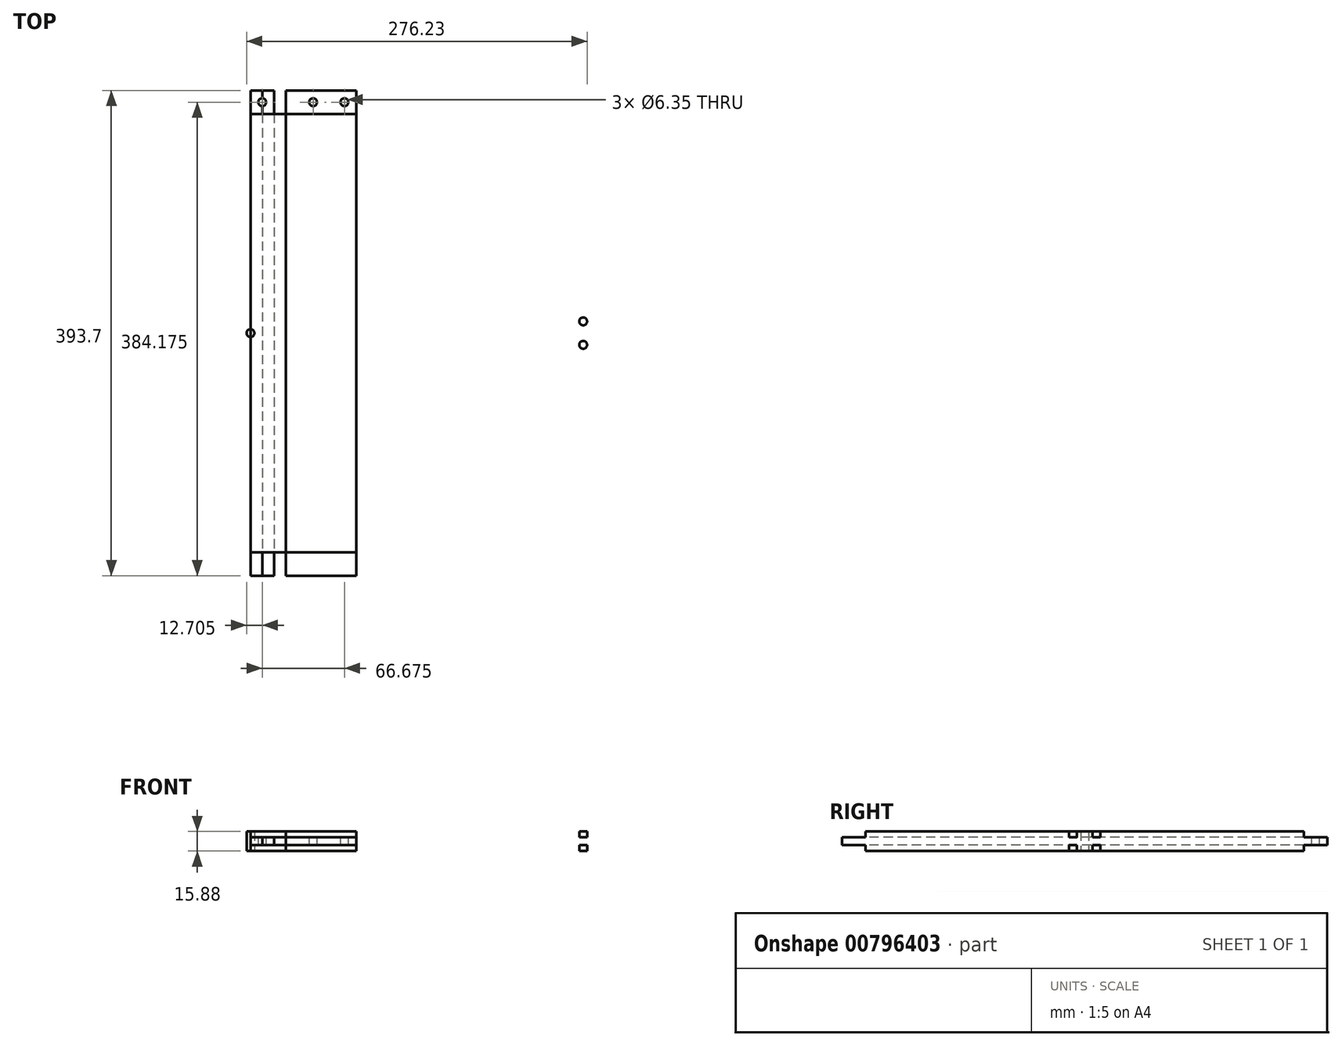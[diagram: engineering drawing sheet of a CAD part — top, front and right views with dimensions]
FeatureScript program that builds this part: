
annotation { "Feature Type Name" : "Feature", "Feature Type Description" : "" }
export const myFeature = defineFeature(function(context is Context, id is Id, definition is map)
    precondition{}
    {
        {
            var Q0;
            Q0=qCreatedBy(makeId("Front.planeOp"),FACE);
            var sketch = newSketch(context, id + "F0", { "sketchPlane" : qUnion([Q0])});
            skLineSegment(sketch, "E0", {"start": v(0, 0) * mm, "end": v(279.4, 0) * mm});
            skLineSegment(sketch, "E1", {"start": v(279.4, 0) * mm, "end": v(279.4, 4.76) * mm});
            skLineSegment(sketch, "E2", {"start": v(279.4, 4.76) * mm, "end": v(203.2, 4.76) * mm});
            skLineSegment(sketch, "E3", {"start": v(203.2, 4.76) * mm, "end": v(203.2, 11.11) * mm});
            skLineSegment(sketch, "E4", {"start": v(203.2, 11.11) * mm, "end": v(279.4, 11.11) * mm});
            skLineSegment(sketch, "E5", {"start": v(279.4, 11.11) * mm, "end": v(279.4, 15.88) * mm});
            skLineSegment(sketch, "E6", {"start": v(279.4, 15.88) * mm, "end": v(0, 15.88) * mm});
            skLineSegment(sketch, "E7.MirrorCS", {"start": v(-279.4, 15.88) * mm, "end": v(0, 15.88) * mm});
            skLineSegment(sketch, "E8.MirrorCS", {"start": v(0, 0) * mm, "end": v(-279.4, 0) * mm});
            skLineSegment(sketch, "E9.MirrorCS", {"start": v(-279.4, 0) * mm, "end": v(-279.4, 4.76) * mm});
            skLineSegment(sketch, "E10.MirrorCS", {"start": v(-279.4, 11.11) * mm, "end": v(-279.4, 15.88) * mm});
            skLineSegment(sketch, "E11", {"start": v(-279.4, 11.11) * mm, "end": v(-260.35, 11.11) * mm});
            skLineSegment(sketch, "E12", {"start": v(-260.35, 11.11) * mm, "end": v(-260.35, 4.76) * mm});
            skLineSegment(sketch, "E13", {"start": v(-279.4, 4.76) * mm, "end": v(-260.35, 4.76) * mm});
            skSolve(sketch);
        }
        {
            var Q0;
            Q0=makeQuery(id+"F0.imprint","IMPRINT",FACE,{"disambiguationData":[TD([[makeQuery(id+"F0.imprint","IMPRINT",EDGE,{"derivedFrom":sQuery(id+"F0.wireOp",EDGE,"E0")}),1.0]])]});
            extrude(context, id + "F1", {"entities" : qUnion([Q0]), "depth" : 19.05 * mm, "offsetDistance" : 25.4 * mm});
        }
        {
            var Q0;
            Q0=makeQuery(id+"F1.opExtrude","SWEPT_FACE",FACE,{"disambiguationData":[OSD([sQuery(id+"F0.wireOp",EDGE,"E12")])]});
            var sketch = newSketch(context, id + "F2", { "sketchPlane" : qUnion([Q0])});
            skLineSegment(sketch, "E14", {"start": v(9.53, 11.11) * mm, "end": v(9.53, 4.76) * mm});
            skSolve(sketch);
        }
        {
            var Q0;
            Q0 = qSketchRegion(id + "F2", true);
            var Q1;
            {var subQ0=sQuery(id+"F2.wireOp",EDGE,"E14");Q1=makeQuery(id+"F2.imprint","IMPRINT",FACE,{"disambiguationData":[TD([[makeQuery(id+"F2.imprint","IMPRINT",EDGE,{"derivedFrom":subQ0}),-1.0]])]});}
            extrude(context, id + "F3", {"entities" : qUnion([Q0, Q1]), "operationType" : NewBodyOperationType.REMOVE, "endBound" : BoundingType.THROUGH_ALL, "oppositeDirection" : true, "depth" : 25.4 * mm, "offsetDistance" : 25.4 * mm});
        }
        {
            var Q0;
            Q0=makeQuery(id+"F1.opExtrude","SWEPT_FACE",FACE,{"disambiguationData":[OSD([sQuery(id+"F0.wireOp",EDGE,"E6"),sQuery(id+"F0.wireOp",EDGE,"E7.MirrorCS")])]});
            var sketch = newSketch(context, id + "F4", { "sketchPlane" : qUnion([Q0])});
            skCircle(sketch, "E15", {"center": v(-269.88, -9.53) * mm, "radius": 3.18 * mm});
            skPoint(sketch, "E15.centerSnap0", {"position": v(-279.4, -9.53) * mm});
            skCircle(sketch, "E16.MirrorC", {"center": v(269.88, -9.53) * mm, "radius": 3.18 * mm});
            skCircle(sketch, "E17", {"center": v(244.48, -9.52) * mm, "radius": 3.18 * mm});
            skCircle(sketch, "E18", {"center": v(219.08, -9.52) * mm, "radius": 3.18 * mm});
            skSolve(sketch);
        }
        {
            var Q0;
            Q0=makeQuery(id+"F4.imprint","IMPRINT",FACE,{"disambiguationData":[TD([[makeQuery(id+"F4.imprint","IMPRINT",EDGE,{"derivedFrom":sQuery(id+"F4.wireOp",EDGE,"E15")}),1.0]])]});
            var Q1;
            Q1=makeQuery(id+"F4.imprint","IMPRINT",FACE,{"disambiguationData":[TD([[makeQuery(id+"F4.imprint","IMPRINT",EDGE,{"derivedFrom":sQuery(id+"F4.wireOp",EDGE,"E16.MirrorC")}),-1.0]])]});
            var Q2;
            Q2=makeQuery(id+"F4.imprint","IMPRINT",FACE,{"disambiguationData":[TD([[makeQuery(id+"F4.imprint","IMPRINT",EDGE,{"derivedFrom":sQuery(id+"F4.wireOp",EDGE,"E17")}),1.0]])]});
            var Q3;
            Q3=makeQuery(id+"F4.imprint","IMPRINT",FACE,{"disambiguationData":[TD([[makeQuery(id+"F4.imprint","IMPRINT",EDGE,{"derivedFrom":sQuery(id+"F4.wireOp",EDGE,"E18")}),1.0]])]});
            extrude(context, id + "F5", {"entities" : qUnion([Q0, Q1, Q2, Q3]), "operationType" : NewBodyOperationType.REMOVE, "endBound" : BoundingType.THROUGH_ALL, "oppositeDirection" : true, "depth" : 25.4 * mm, "offsetDistance" : 25.4 * mm});
        }
        {
            var Q0;
            Q0=qCreatedBy(makeId("Right.planeOp"),FACE);
            var sketch = newSketch(context, id + "F6", { "sketchPlane" : qUnion([Q0])});
            skLineSegment(sketch, "E19", {"start": v(0, 0) * mm, "end": v(177.8, 0) * mm});
            skLineSegment(sketch, "E20", {"start": v(177.8, 0) * mm, "end": v(177.8, 4.76) * mm});
            skLineSegment(sketch, "E21", {"start": v(177.8, 4.76) * mm, "end": v(196.85, 4.76) * mm});
            skLineSegment(sketch, "E22", {"start": v(196.85, 4.76) * mm, "end": v(196.85, 11.11) * mm});
            skLineSegment(sketch, "E23", {"start": v(196.85, 11.11) * mm, "end": v(177.8, 11.11) * mm});
            skLineSegment(sketch, "E24", {"start": v(177.8, 11.11) * mm, "end": v(177.8, 15.88) * mm});
            skLineSegment(sketch, "E25", {"start": v(177.8, 15.88) * mm, "end": v(0, 15.88) * mm});
            skLineSegment(sketch, "E26.MirrorCS", {"start": v(-177.8, 15.88) * mm, "end": v(0, 15.88) * mm});
            skLineSegment(sketch, "E27.MirrorCS", {"start": v(0, 0) * mm, "end": v(-177.8, 0) * mm});
            skLineSegment(sketch, "E28.MirrorCS", {"start": v(-177.8, 0) * mm, "end": v(-177.8, 4.76) * mm});
            skLineSegment(sketch, "E29.MirrorCS", {"start": v(-177.8, 4.76) * mm, "end": v(-196.85, 4.76) * mm});
            skLineSegment(sketch, "E30.MirrorCS", {"start": v(-196.85, 4.76) * mm, "end": v(-196.85, 11.11) * mm});
            skLineSegment(sketch, "E31.MirrorCS", {"start": v(-196.85, 11.11) * mm, "end": v(-177.8, 11.11) * mm});
            skLineSegment(sketch, "E32.MirrorCS", {"start": v(-177.8, 11.11) * mm, "end": v(-177.8, 15.88) * mm});
            skSolve(sketch);
        }
        {
            var Q0;
            Q0=makeQuery(id+"F6.imprint","IMPRINT",FACE,{"disambiguationData":[TD([[makeQuery(id+"F6.imprint","IMPRINT",EDGE,{"derivedFrom":sQuery(id+"F6.wireOp",EDGE,"E19")}),1.0]])]});
            extrude(context, id + "F7", {"entities" : qUnion([Q0]), "depth" : 85.72 * mm, "offsetDistance" : 25.4 * mm});
        }
        {
            var Q0;
            Q0=makeQuery(id+"F7.opExtrude","SWEPT_FACE",FACE,{"disambiguationData":[OSD([sQuery(id+"F6.wireOp",EDGE,"E23")])]});
            var sketch = newSketch(context, id + "F8", { "sketchPlane" : qUnion([Q0])});
            skCircle(sketch, "E33", {"center": v(76.2, 187.33) * mm, "radius": 3.18 * mm});
            skPoint(sketch, "E33.centerSnap0", {"position": v(85.73, 187.33) * mm});
            skPoint(sketch, "E33.centerSnap1", {"position": v(76.2, 196.85) * mm});
            skCircle(sketch, "E34.MirrorC", {"center": v(76.2, -187.33) * mm, "radius": 3.18 * mm});
            skCircle(sketch, "E35", {"center": v(50.8, 187.33) * mm, "radius": 3.18 * mm});
            skCircle(sketch, "E36.MirrorC", {"center": v(50.8, -187.33) * mm, "radius": 3.18 * mm});
            skCircle(sketch, "E37", {"center": v(25.4, 187.33) * mm, "radius": 3.18 * mm});
            skCircle(sketch, "E38.MirrorC", {"center": v(25.4, -187.33) * mm, "radius": 3.18 * mm});
            skSolve(sketch);
        }
        {
            var Q0;
            Q0=makeQuery(id+"F8.imprint","IMPRINT",FACE,{"disambiguationData":[TD([[makeQuery(id+"F8.imprint","IMPRINT",EDGE,{"derivedFrom":sQuery(id+"F8.wireOp",EDGE,"E33")}),1.0]])]});
            var Q1;
            Q1=makeQuery(id+"F8.imprint","IMPRINT",FACE,{"disambiguationData":[TD([[makeQuery(id+"F8.imprint","IMPRINT",EDGE,{"derivedFrom":sQuery(id+"F8.wireOp",EDGE,"E34.MirrorC")}),-1.0]])]});
            var Q2;
            Q2=makeQuery(id+"F8.imprint","IMPRINT",FACE,{"disambiguationData":[TD([[makeQuery(id+"F8.imprint","IMPRINT",EDGE,{"derivedFrom":sQuery(id+"F8.wireOp",EDGE,"E35")}),1.0]])]});
            var Q3;
            Q3=makeQuery(id+"F8.imprint","IMPRINT",FACE,{"disambiguationData":[TD([[makeQuery(id+"F8.imprint","IMPRINT",EDGE,{"derivedFrom":sQuery(id+"F8.wireOp",EDGE,"E36.MirrorC")}),-1.0]])]});
            var Q4;
            Q4=makeQuery(id+"F8.imprint","IMPRINT",FACE,{"disambiguationData":[TD([[makeQuery(id+"F8.imprint","IMPRINT",EDGE,{"derivedFrom":sQuery(id+"F8.wireOp",EDGE,"E37")}),1.0]])]});
            var Q5;
            Q5=makeQuery(id+"F8.imprint","IMPRINT",FACE,{"disambiguationData":[TD([[makeQuery(id+"F8.imprint","IMPRINT",EDGE,{"derivedFrom":sQuery(id+"F8.wireOp",EDGE,"E38.MirrorC")}),-1.0]])]});
            extrude(context, id + "F9", {"entities" : qUnion([Q0, Q1, Q2, Q3, Q4, Q5]), "operationType" : NewBodyOperationType.REMOVE, "endBound" : BoundingType.THROUGH_ALL, "oppositeDirection" : true, "depth" : 25.4 * mm, "offsetDistance" : 25.4 * mm});
        }
        {
            var Q0;
            Q0=makeQuery(id+"F7.opExtrude","SWEPT_FACE",FACE,{"disambiguationData":[OSD([sQuery(id+"F6.wireOp",EDGE,"E30.MirrorCS")])]});
            var sketch = newSketch(context, id + "F10", { "sketchPlane" : qUnion([Q0])});
            skLineSegment(sketch, "E39", {"start": v(9.53, 11.11) * mm, "end": v(9.53, 4.76) * mm});
            skSolve(sketch);
        }
        {
            var Q0;
            {var subQ0=sQuery(id+"F10.wireOp",EDGE,"E39");Q0=makeQuery(id+"F10.imprint","IMPRINT",FACE,{"disambiguationData":[TD([[makeQuery(id+"F10.imprint","IMPRINT",EDGE,{"derivedFrom":subQ0}),-1.0]])]});}
            extrude(context, id + "F11", {"entities" : qUnion([Q0]), "operationType" : NewBodyOperationType.REMOVE, "endBound" : BoundingType.THROUGH_ALL, "oppositeDirection" : true, "depth" : 25.4 * mm, "offsetDistance" : 25.4 * mm});
        }
        {
            var Q0;
            Q0=makeQuery(id+"F1.opExtrude","SWEPT_BODY",BODY,{"disambiguationData":[OSD([sQuery(id+"F0.wireOp",EDGE,"E0"),sQuery(id+"F0.wireOp",EDGE,"E1"),sQuery(id+"F0.wireOp",EDGE,"E2"),sQuery(id+"F0.wireOp",EDGE,"E3"),sQuery(id+"F0.wireOp",EDGE,"E4"),sQuery(id+"F0.wireOp",EDGE,"E5"),sQuery(id+"F0.wireOp",EDGE,"E6"),sQuery(id+"F0.wireOp",EDGE,"E7.MirrorCS"),sQuery(id+"F0.wireOp",EDGE,"E8.MirrorCS"),sQuery(id+"F0.wireOp",EDGE,"E9.MirrorCS"),sQuery(id+"F0.wireOp",EDGE,"E10.MirrorCS"),sQuery(id+"F0.wireOp",EDGE,"E11"),sQuery(id+"F0.wireOp",EDGE,"E12"),sQuery(id+"F0.wireOp",EDGE,"E13")])]});
            var Q1;
            Q1=qCreatedBy(makeId("Front.planeOp"),FACE);
            mirror(context, id + "F12", {"entities" : qUnion([Q0]), "mirrorPlane" : qUnion([Q1])});
        }
        {
            var Q0;
            Q0=qCreatedBy(makeId("Right.planeOp"),FACE);
            var sketch = newSketch(context, id + "F13", { "sketchPlane" : qUnion([Q0])});
            skLineSegment(sketch, "E40", {"start": v(0, 0) * mm, "end": v(177.8, 0) * mm});
            skLineSegment(sketch, "E41", {"start": v(177.8, 0) * mm, "end": v(177.8, 4.76) * mm});
            skLineSegment(sketch, "E42", {"start": v(177.8, 4.76) * mm, "end": v(196.85, 4.76) * mm});
            skLineSegment(sketch, "E43", {"start": v(196.85, 4.76) * mm, "end": v(196.85, 11.11) * mm});
            skLineSegment(sketch, "E44", {"start": v(196.85, 11.11) * mm, "end": v(177.8, 11.11) * mm});
            skLineSegment(sketch, "E45", {"start": v(177.8, 11.11) * mm, "end": v(177.8, 15.88) * mm});
            skLineSegment(sketch, "E46", {"start": v(177.8, 15.88) * mm, "end": v(0, 15.88) * mm});
            skLineSegment(sketch, "E47.MirrorCS", {"start": v(-177.8, 15.88) * mm, "end": v(0, 15.88) * mm});
            skLineSegment(sketch, "E48.MirrorCS", {"start": v(0, 0) * mm, "end": v(-177.8, 0) * mm});
            skLineSegment(sketch, "E49.MirrorCS", {"start": v(-177.8, 0) * mm, "end": v(-177.8, 4.76) * mm});
            skLineSegment(sketch, "E50.MirrorCS", {"start": v(-177.8, 4.76) * mm, "end": v(-196.85, 4.76) * mm});
            skLineSegment(sketch, "E51.MirrorCS", {"start": v(-196.85, 4.76) * mm, "end": v(-196.85, 11.11) * mm});
            skLineSegment(sketch, "E52.MirrorCS", {"start": v(-196.85, 11.11) * mm, "end": v(-177.8, 11.11) * mm});
            skLineSegment(sketch, "E53.MirrorCS", {"start": v(-177.8, 11.11) * mm, "end": v(-177.8, 15.88) * mm});
            skSolve(sketch);
        }
        {
            var Q0;
            Q0=makeQuery(id+"F13.imprint","IMPRINT",FACE,{"disambiguationData":[TD([[makeQuery(id+"F13.imprint","IMPRINT",EDGE,{"derivedFrom":sQuery(id+"F13.wireOp",EDGE,"E40")}),1.0]])]});
            extrude(context, id + "F14", {"entities" : qUnion([Q0]), "depth" : 28.57 * mm, "offsetDistance" : 25.4 * mm});
        }
        {
            var Q0;
            Q0=makeQuery(id+"F14.opExtrude","SWEPT_FACE",FACE,{"disambiguationData":[OSD([sQuery(id+"F13.wireOp",EDGE,"E51.MirrorCS")])]});
            var sketch = newSketch(context, id + "F15", { "sketchPlane" : qUnion([Q0])});
            skLineSegment(sketch, "E54", {"start": v(19.05, 11.11) * mm, "end": v(19.05, 4.76) * mm});
            skSolve(sketch);
        }
        {
            var Q0;
            {var subQ0=sQuery(id+"F15.wireOp",EDGE,"E54");Q0=makeQuery(id+"F15.imprint","IMPRINT",FACE,{"disambiguationData":[TD([[makeQuery(id+"F15.imprint","IMPRINT",EDGE,{"derivedFrom":subQ0}),1.0]])]});}
            extrude(context, id + "F16", {"entities" : qUnion([Q0]), "operationType" : NewBodyOperationType.REMOVE, "endBound" : BoundingType.THROUGH_ALL, "oppositeDirection" : true, "depth" : 25.4 * mm, "offsetDistance" : 25.4 * mm});
        }
        {
            var Q0;
            Q0=makeQuery(id+"F14.opExtrude","SWEPT_FACE",FACE,{"disambiguationData":[OSD([sQuery(id+"F13.wireOp",EDGE,"E44")])]});
            var sketch = newSketch(context, id + "F17", { "sketchPlane" : qUnion([Q0])});
            skCircle(sketch, "E55", {"center": v(9.53, 187.33) * mm, "radius": 3.18 * mm});
            skPoint(sketch, "E55.centerSnap0", {"position": v(0, 187.33) * mm});
            skPoint(sketch, "E55.centerSnap1", {"position": v(9.53, 196.85) * mm});
            skCircle(sketch, "E56.MirrorC", {"center": v(9.53, -187.33) * mm, "radius": 3.18 * mm});
            skSolve(sketch);
        }
        {
            var Q0;
            Q0=makeQuery(id+"F17.imprint","IMPRINT",FACE,{"disambiguationData":[TD([[makeQuery(id+"F17.imprint","IMPRINT",EDGE,{"derivedFrom":sQuery(id+"F17.wireOp",EDGE,"E55")}),1.0]])]});
            var Q1;
            Q1=makeQuery(id+"F17.imprint","IMPRINT",FACE,{"disambiguationData":[TD([[makeQuery(id+"F17.imprint","IMPRINT",EDGE,{"derivedFrom":sQuery(id+"F17.wireOp",EDGE,"E56.MirrorC")}),-1.0]])]});
            extrude(context, id + "F18", {"entities" : qUnion([Q0, Q1]), "operationType" : NewBodyOperationType.REMOVE, "endBound" : BoundingType.THROUGH_ALL, "oppositeDirection" : true, "depth" : 25.4 * mm, "offsetDistance" : 25.4 * mm});
        }
        {
            var Q0;
            Q0=qCreatedBy(makeId("Top.planeOp"),FACE);
            var sketch = newSketch(context, id + "F19", { "sketchPlane" : qUnion([Q0])});
            skCircle(sketch, "E57", {"center": v(0, 0) * mm, "radius": 3.18 * mm});
            skSolve(sketch);
        }
        {
            var Q0;
            Q0=makeQuery(id+"F19.imprint","IMPRINT",FACE,{"disambiguationData":[TD([[makeQuery(id+"F19.imprint","IMPRINT",EDGE,{"derivedFrom":sQuery(id+"F19.wireOp",EDGE,"E57")}),1.0]])]});
            extrude(context, id + "F20", {"entities" : qUnion([Q0]), "depth" : 15.88 * mm, "offsetDistance" : 25.4 * mm});
        }
    });
